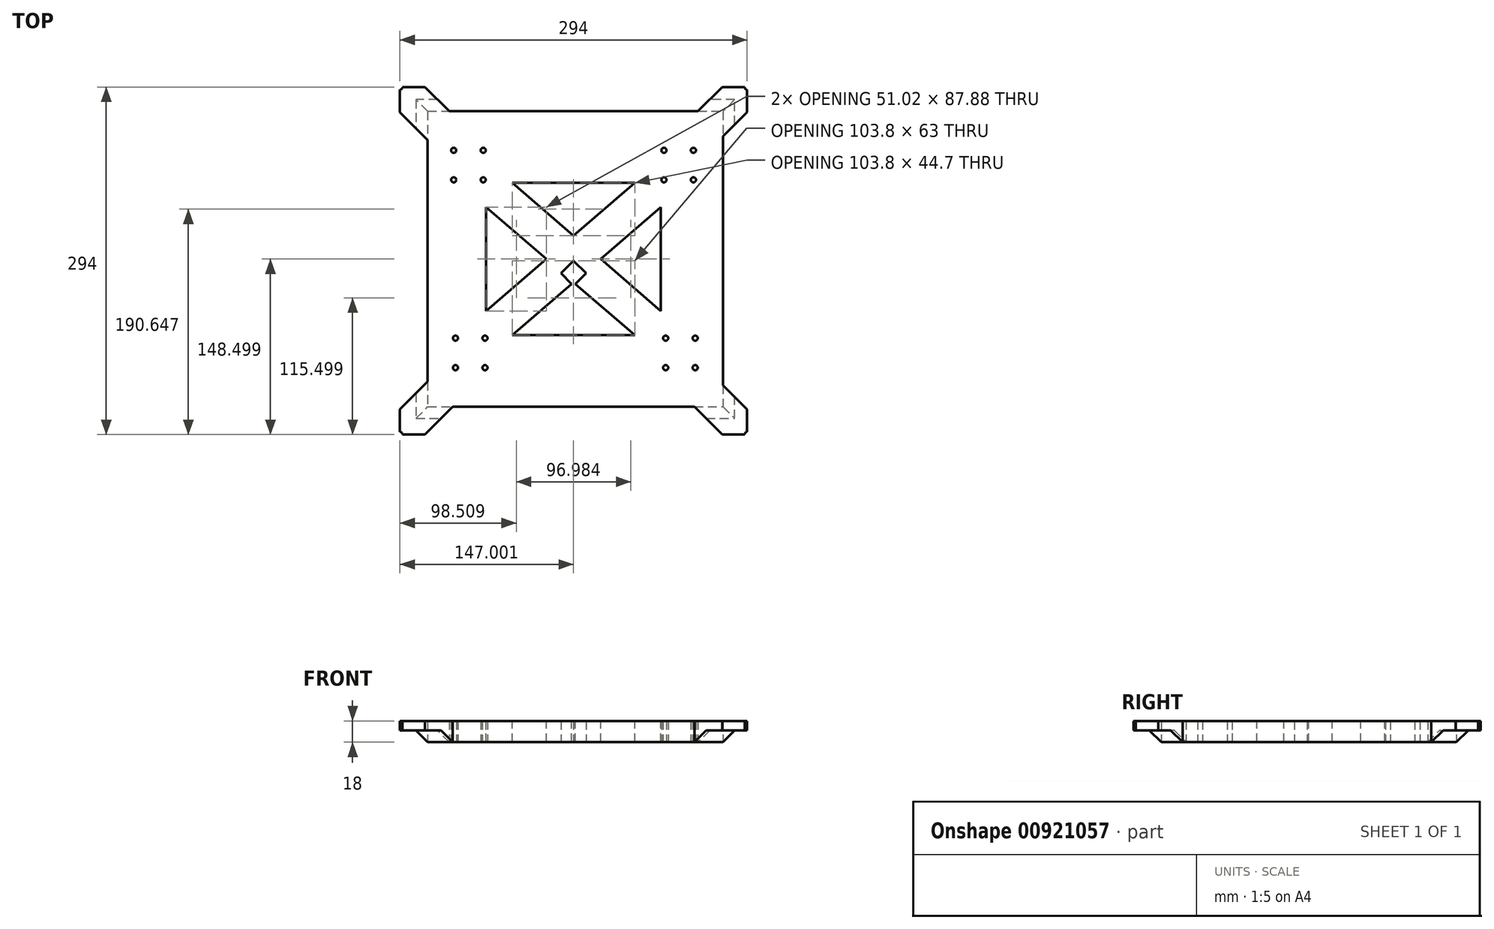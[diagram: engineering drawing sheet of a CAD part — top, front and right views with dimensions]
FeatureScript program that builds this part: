
annotation { "Feature Type Name" : "Feature", "Feature Type Description" : "" }
export const myFeature = defineFeature(function(context is Context, id is Id, definition is map)
    precondition{}
    {
        {
            var Q0;
            Q0=qCreatedBy(makeId("Top.planeOp"),FACE);
            var sketch = newSketch(context, id + "F0", { "sketchPlane" : qUnion([Q0])});
            skLineSegment(sketch, "E0.bottom", {"start": v(-132.57, 169.64) * mm, "end": v(117.43, 169.64) * mm});
            skLineSegment(sketch, "E0.top", {"start": v(-132.57, -80.36) * mm, "end": v(117.43, -80.36) * mm});
            skLineSegment(sketch, "E0.left", {"start": v(-132.57, 169.64) * mm, "end": v(-132.57, -80.36) * mm});
            skLineSegment(sketch, "E0.right", {"start": v(117.43, 169.64) * mm, "end": v(117.43, -80.36) * mm});
            skLineSegment(sketch, "E1", {"start": v(-9.07, 43.14) * mm, "end": v(137.93, 190.14) * mm});
            skLineSegment(sketch, "E2", {"start": v(-9.07, 43.14) * mm, "end": v(137.93, -103.86) * mm});
            skLineSegment(sketch, "E3", {"start": v(137.93, -103.86) * mm, "end": v(137.93, 190.14) * mm});
            skLineSegment(sketch, "E4", {"start": v(-9.07, 43.14) * mm, "end": v(-156.07, 190.14) * mm});
            skLineSegment(sketch, "E5", {"start": v(-156.07, 190.14) * mm, "end": v(137.93, 190.14) * mm});
            skLineSegment(sketch, "E6", {"start": v(-9.07, 43.14) * mm, "end": v(-156.07, -103.86) * mm});
            skLineSegment(sketch, "E7", {"start": v(-156.07, -103.86) * mm, "end": v(-156.07, 190.14) * mm});
            skLineSegment(sketch, "E8", {"start": v(-156.07, -103.86) * mm, "end": v(137.93, -103.86) * mm});
            skArc(sketch, "E9.0.startCap", {"start": v(1.54, 53.75) * mm, "mid": v(1.54, 32.53) * mm, "end": v(-19.68, 32.53) * mm});
            skArc(sketch, "E9.0.endCap", {"start": v(-166.68, 179.53) * mm, "mid": v(-166.68, 200.75) * mm, "end": v(-145.46, 200.75) * mm});
            skLineSegment(sketch, "E9.0.left", {"start": v(-19.68, 32.53) * mm, "end": v(-166.68, 179.53) * mm});
            skLineSegment(sketch, "E9.0.right", {"start": v(1.54, 53.75) * mm, "end": v(-145.46, 200.75) * mm});
            skArc(sketch, "E10.0.startCap", {"start": v(1.54, 32.53) * mm, "mid": v(-19.68, 32.53) * mm, "end": v(-19.68, 53.75) * mm});
            skArc(sketch, "E10.0.endCap", {"start": v(127.32, 200.75) * mm, "mid": v(148.54, 200.75) * mm, "end": v(148.54, 179.53) * mm});
            skLineSegment(sketch, "E10.0.left", {"start": v(-19.68, 53.75) * mm, "end": v(127.32, 200.75) * mm});
            skLineSegment(sketch, "E10.0.right", {"start": v(1.54, 32.53) * mm, "end": v(148.54, 179.53) * mm});
            skArc(sketch, "E11.0.startCap", {"start": v(-19.68, 32.53) * mm, "mid": v(-19.68, 53.75) * mm, "end": v(1.54, 53.75) * mm});
            skArc(sketch, "E11.0.endCap", {"start": v(148.54, -93.25) * mm, "mid": v(148.54, -114.47) * mm, "end": v(127.32, -114.47) * mm});
            skLineSegment(sketch, "E11.0.left", {"start": v(1.54, 53.75) * mm, "end": v(148.54, -93.25) * mm});
            skLineSegment(sketch, "E11.0.right", {"start": v(-19.68, 32.53) * mm, "end": v(127.32, -114.47) * mm});
            skArc(sketch, "E11.1.startCap", {"start": v(-19.68, 53.75) * mm, "mid": v(1.54, 53.75) * mm, "end": v(1.54, 32.53) * mm});
            skArc(sketch, "E11.1.endCap", {"start": v(-145.46, -114.47) * mm, "mid": v(-166.68, -114.47) * mm, "end": v(-166.68, -93.25) * mm});
            skLineSegment(sketch, "E11.1.left", {"start": v(1.54, 32.53) * mm, "end": v(-145.46, -114.47) * mm});
            skLineSegment(sketch, "E11.1.right", {"start": v(-19.68, 53.75) * mm, "end": v(-166.68, -93.25) * mm});
            skSolve(sketch);
        }
        {
            var Q0;
            {var subQ1=sQuery(id+"F0.wireOp",EDGE,"E0.bottom");var subQ3=sQuery(id+"F0.wireOp",EDGE,"E9.0.right");var subQ4=makeQuery(id+"F0.imprint","INTERSECT",VERTEX,{"derivedFrom":[subQ1,subQ3]});Q0=makeQuery(id+"F0.imprint","IMPRINT",FACE,{"disambiguationData":[TD([[makeQuery(id+"F0.imprint","IMPRINT",EDGE,{"disambiguationData":[TD([[subQ4,1.0]])],"derivedFrom":subQ3}),1.0]])]});}
            var Q1;
            {var subQ1=sQuery(id+"F0.wireOp",EDGE,"E0.left");var subQ3=sQuery(id+"F0.wireOp",EDGE,"E9.0.left");var subQ4=makeQuery(id+"F0.imprint","INTERSECT",VERTEX,{"derivedFrom":[subQ1,subQ3]});Q1=makeQuery(id+"F0.imprint","IMPRINT",FACE,{"disambiguationData":[TD([[makeQuery(id+"F0.imprint","IMPRINT",EDGE,{"disambiguationData":[TD([[subQ4,1.0]])],"derivedFrom":subQ3}),-1.0]])]});}
            var Q2;
            {var subQ1=sQuery(id+"F0.wireOp",EDGE,"E0.bottom");var subQ3=sQuery(id+"F0.wireOp",EDGE,"E10.0.left");var subQ4=makeQuery(id+"F0.imprint","INTERSECT",VERTEX,{"derivedFrom":[subQ1,subQ3]});Q2=makeQuery(id+"F0.imprint","IMPRINT",FACE,{"disambiguationData":[TD([[makeQuery(id+"F0.imprint","IMPRINT",EDGE,{"disambiguationData":[TD([[subQ4,1.0]])],"derivedFrom":subQ3}),-1.0]])]});}
            var Q3;
            {var subQ1=sQuery(id+"F0.wireOp",EDGE,"E0.right");var subQ3=sQuery(id+"F0.wireOp",EDGE,"E10.0.right");var subQ4=makeQuery(id+"F0.imprint","INTERSECT",VERTEX,{"derivedFrom":[subQ1,subQ3]});Q3=makeQuery(id+"F0.imprint","IMPRINT",FACE,{"disambiguationData":[TD([[makeQuery(id+"F0.imprint","IMPRINT",EDGE,{"disambiguationData":[TD([[subQ4,1.0]])],"derivedFrom":subQ3}),1.0]])]});}
            var Q4;
            {var subQ1=sQuery(id+"F0.wireOp",EDGE,"E0.top");var subQ3=sQuery(id+"F0.wireOp",EDGE,"E11.0.right");var subQ4=makeQuery(id+"F0.imprint","INTERSECT",VERTEX,{"derivedFrom":[subQ1,subQ3]});Q4=makeQuery(id+"F0.imprint","IMPRINT",FACE,{"disambiguationData":[TD([[makeQuery(id+"F0.imprint","IMPRINT",EDGE,{"disambiguationData":[TD([[subQ4,1.0]])],"derivedFrom":subQ3}),1.0]])]});}
            var Q5;
            {var subQ1=sQuery(id+"F0.wireOp",EDGE,"E0.right");var subQ3=sQuery(id+"F0.wireOp",EDGE,"E11.0.left");var subQ4=makeQuery(id+"F0.imprint","INTERSECT",VERTEX,{"derivedFrom":[subQ1,subQ3]});Q5=makeQuery(id+"F0.imprint","IMPRINT",FACE,{"disambiguationData":[TD([[makeQuery(id+"F0.imprint","IMPRINT",EDGE,{"disambiguationData":[TD([[subQ4,1.0]])],"derivedFrom":subQ3}),-1.0]])]});}
            var Q6;
            {var subQ0=sQuery(id+"F0.wireOp",EDGE,"E10.0.startCap");Q6=makeQuery(id+"F0.imprint","IMPRINT",FACE,{"disambiguationData":[TD([[makeQuery(id+"F0.imprint","IMPRINT",EDGE,{"derivedFrom":subQ0}),1.0]])]});}
            var Q7;
            {var subQ3=sQuery(id+"F0.wireOp",EDGE,"E11.0.startCap");Q7=makeQuery(id+"F0.imprint","IMPRINT",FACE,{"disambiguationData":[TD([[makeQuery(id+"F0.imprint","IMPRINT",EDGE,{"derivedFrom":subQ3}),-1.0]])]});}
            var Q8;
            {var subQ1=sQuery(id+"F0.wireOp",EDGE,"E9.0.right");var subQ3=sQuery(id+"F0.wireOp",EDGE,"E10.0.left");var subQ4=makeQuery(id+"F0.imprint","INTERSECT",VERTEX,{"derivedFrom":[subQ1,subQ3]});Q8=makeQuery(id+"F0.imprint","IMPRINT",FACE,{"disambiguationData":[TD([[makeQuery(id+"F0.imprint","IMPRINT",EDGE,{"disambiguationData":[TD([[subQ4,1.0]])],"derivedFrom":subQ1}),1.0]])]});}
            var Q9;
            {var subQ0=sQuery(id+"F0.wireOp",EDGE,"E2");var subQ1=sQuery(id+"F0.wireOp",EDGE,"E1");var subQ2=makeQuery(id+"F0.imprint","INTERSECT",VERTEX,{"derivedFrom":[subQ1,subQ0,sQuery(id+"F0.wireOp",EDGE,"E4"),sQuery(id+"F0.wireOp",EDGE,"E6")]});Q9=makeQuery(id+"F0.imprint","IMPRINT",FACE,{"disambiguationData":[TD([[makeQuery(id+"F0.imprint","IMPRINT",EDGE,{"disambiguationData":[TD([[subQ2,-1.0]])],"derivedFrom":subQ1}),-1.0]])]});}
            var Q10;
            {var subQ3=sQuery(id+"F0.wireOp",EDGE,"E10.0.startCap");Q10=makeQuery(id+"F0.imprint","IMPRINT",FACE,{"disambiguationData":[TD([[makeQuery(id+"F0.imprint","IMPRINT",EDGE,{"derivedFrom":subQ3}),-1.0]])]});}
            var Q11;
            {var subQ0=sQuery(id+"F0.wireOp",EDGE,"E4");var subQ1=sQuery(id+"F0.wireOp",EDGE,"E1");var subQ2=makeQuery(id+"F0.imprint","INTERSECT",VERTEX,{"derivedFrom":[subQ1,sQuery(id+"F0.wireOp",EDGE,"E2"),subQ0,sQuery(id+"F0.wireOp",EDGE,"E6")]});Q11=makeQuery(id+"F0.imprint","IMPRINT",FACE,{"disambiguationData":[TD([[makeQuery(id+"F0.imprint","IMPRINT",EDGE,{"disambiguationData":[TD([[subQ2,-1.0]])],"derivedFrom":subQ1}),1.0]])]});}
            var Q12;
            {var subQ1=sQuery(id+"F0.wireOp",EDGE,"E10.0.right");var subQ3=sQuery(id+"F0.wireOp",EDGE,"E11.0.left");var subQ4=makeQuery(id+"F0.imprint","INTERSECT",VERTEX,{"derivedFrom":[subQ1,subQ3]});Q12=makeQuery(id+"F0.imprint","IMPRINT",FACE,{"disambiguationData":[TD([[makeQuery(id+"F0.imprint","IMPRINT",EDGE,{"disambiguationData":[TD([[subQ4,1.0]])],"derivedFrom":subQ3}),-1.0]])]});}
            var Q13;
            {var subQ0=sQuery(id+"F0.wireOp",EDGE,"E11.0.startCap");Q13=makeQuery(id+"F0.imprint","IMPRINT",FACE,{"disambiguationData":[TD([[makeQuery(id+"F0.imprint","IMPRINT",EDGE,{"derivedFrom":subQ0}),1.0]])]});}
            var Q14;
            {var subQ1=sQuery(id+"F0.wireOp",EDGE,"E0.top");var subQ3=sQuery(id+"F0.wireOp",EDGE,"E11.1.left");var subQ4=makeQuery(id+"F0.imprint","INTERSECT",VERTEX,{"derivedFrom":[subQ1,subQ3]});Q14=makeQuery(id+"F0.imprint","IMPRINT",FACE,{"disambiguationData":[TD([[makeQuery(id+"F0.imprint","IMPRINT",EDGE,{"disambiguationData":[TD([[subQ4,1.0]])],"derivedFrom":subQ3}),-1.0]])]});}
            var Q15;
            {var subQ1=sQuery(id+"F0.wireOp",EDGE,"E0.left");var subQ3=sQuery(id+"F0.wireOp",EDGE,"E11.1.right");var subQ4=makeQuery(id+"F0.imprint","INTERSECT",VERTEX,{"derivedFrom":[subQ1,subQ3]});Q15=makeQuery(id+"F0.imprint","IMPRINT",FACE,{"disambiguationData":[TD([[makeQuery(id+"F0.imprint","IMPRINT",EDGE,{"disambiguationData":[TD([[subQ4,1.0]])],"derivedFrom":subQ3}),1.0]])]});}
            var Q16;
            {var subQ1=sQuery(id+"F0.wireOp",EDGE,"E9.0.endCap");Q16=makeQuery(id+"F0.imprint","IMPRINT",FACE,{"disambiguationData":[TD([[makeQuery(id+"F0.imprint","IMPRINT",EDGE,{"derivedFrom":subQ1}),-1.0]])]});}
            var Q17;
            {var subQ3=sQuery(id+"F0.wireOp",EDGE,"E9.0.left");var subQ5=sQuery(id+"F0.wireOp",EDGE,"E7");var subQ7=makeQuery(id+"F0.imprint","INTERSECT",VERTEX,{"derivedFrom":[subQ5,subQ3]});Q17=makeQuery(id+"F0.imprint","IMPRINT",FACE,{"disambiguationData":[TD([[makeQuery(id+"F0.imprint","IMPRINT",EDGE,{"disambiguationData":[TD([[subQ7,1.0]])],"derivedFrom":subQ3}),-1.0]])]});}
            var Q18;
            {var subQ3=sQuery(id+"F0.wireOp",EDGE,"E9.0.right");var subQ5=sQuery(id+"F0.wireOp",EDGE,"E5");var subQ7=makeQuery(id+"F0.imprint","INTERSECT",VERTEX,{"derivedFrom":[subQ5,subQ3]});Q18=makeQuery(id+"F0.imprint","IMPRINT",FACE,{"disambiguationData":[TD([[makeQuery(id+"F0.imprint","IMPRINT",EDGE,{"disambiguationData":[TD([[subQ7,1.0]])],"derivedFrom":subQ3}),1.0]])]});}
            var Q19;
            {var subQ0=sQuery(id+"F0.wireOp",EDGE,"E10.0.endCap");Q19=makeQuery(id+"F0.imprint","IMPRINT",FACE,{"disambiguationData":[TD([[makeQuery(id+"F0.imprint","IMPRINT",EDGE,{"derivedFrom":subQ0}),-1.0]])]});}
            var Q20;
            {var subQ3=sQuery(id+"F0.wireOp",EDGE,"E10.0.left");var subQ5=sQuery(id+"F0.wireOp",EDGE,"E5");var subQ7=makeQuery(id+"F0.imprint","INTERSECT",VERTEX,{"derivedFrom":[subQ5,subQ3]});Q20=makeQuery(id+"F0.imprint","IMPRINT",FACE,{"disambiguationData":[TD([[makeQuery(id+"F0.imprint","IMPRINT",EDGE,{"disambiguationData":[TD([[subQ7,1.0]])],"derivedFrom":subQ3}),-1.0]])]});}
            var Q21;
            {var subQ3=sQuery(id+"F0.wireOp",EDGE,"E10.0.right");var subQ5=sQuery(id+"F0.wireOp",EDGE,"E3");var subQ7=makeQuery(id+"F0.imprint","INTERSECT",VERTEX,{"derivedFrom":[subQ5,subQ3]});Q21=makeQuery(id+"F0.imprint","IMPRINT",FACE,{"disambiguationData":[TD([[makeQuery(id+"F0.imprint","IMPRINT",EDGE,{"disambiguationData":[TD([[subQ7,1.0]])],"derivedFrom":subQ3}),1.0]])]});}
            var Q22;
            {var subQ3=sQuery(id+"F0.wireOp",EDGE,"E11.0.left");var subQ5=sQuery(id+"F0.wireOp",EDGE,"E3");var subQ7=makeQuery(id+"F0.imprint","INTERSECT",VERTEX,{"derivedFrom":[subQ5,subQ3]});Q22=makeQuery(id+"F0.imprint","IMPRINT",FACE,{"disambiguationData":[TD([[makeQuery(id+"F0.imprint","IMPRINT",EDGE,{"disambiguationData":[TD([[subQ7,1.0]])],"derivedFrom":subQ3}),-1.0]])]});}
            var Q23;
            {var subQ3=sQuery(id+"F0.wireOp",EDGE,"E11.0.right");var subQ5=sQuery(id+"F0.wireOp",EDGE,"E8");var subQ7=makeQuery(id+"F0.imprint","INTERSECT",VERTEX,{"derivedFrom":[subQ5,subQ3]});Q23=makeQuery(id+"F0.imprint","IMPRINT",FACE,{"disambiguationData":[TD([[makeQuery(id+"F0.imprint","IMPRINT",EDGE,{"disambiguationData":[TD([[subQ7,1.0]])],"derivedFrom":subQ3}),1.0]])]});}
            var Q24;
            {var subQ0=sQuery(id+"F0.wireOp",EDGE,"E11.0.endCap");Q24=makeQuery(id+"F0.imprint","IMPRINT",FACE,{"disambiguationData":[TD([[makeQuery(id+"F0.imprint","IMPRINT",EDGE,{"derivedFrom":subQ0}),-1.0]])]});}
            var Q25;
            {var subQ1=sQuery(id+"F0.wireOp",EDGE,"E11.1.endCap");Q25=makeQuery(id+"F0.imprint","IMPRINT",FACE,{"disambiguationData":[TD([[makeQuery(id+"F0.imprint","IMPRINT",EDGE,{"derivedFrom":subQ1}),-1.0]])]});}
            var Q26;
            {var subQ3=sQuery(id+"F0.wireOp",EDGE,"E11.1.left");var subQ5=sQuery(id+"F0.wireOp",EDGE,"E8");var subQ7=makeQuery(id+"F0.imprint","INTERSECT",VERTEX,{"derivedFrom":[subQ5,subQ3]});Q26=makeQuery(id+"F0.imprint","IMPRINT",FACE,{"disambiguationData":[TD([[makeQuery(id+"F0.imprint","IMPRINT",EDGE,{"disambiguationData":[TD([[subQ7,1.0]])],"derivedFrom":subQ3}),-1.0]])]});}
            var Q27;
            {var subQ3=sQuery(id+"F0.wireOp",EDGE,"E11.1.right");var subQ5=sQuery(id+"F0.wireOp",EDGE,"E7");var subQ7=makeQuery(id+"F0.imprint","INTERSECT",VERTEX,{"derivedFrom":[subQ5,subQ3]});Q27=makeQuery(id+"F0.imprint","IMPRINT",FACE,{"disambiguationData":[TD([[makeQuery(id+"F0.imprint","IMPRINT",EDGE,{"disambiguationData":[TD([[subQ7,1.0]])],"derivedFrom":subQ3}),1.0]])]});}
            var Q28;
            {var subQ0=sQuery(id+"F0.wireOp",EDGE,"E10.0.right");var subQ1=sQuery(id+"F0.wireOp",EDGE,"E0.right");var subQ2=makeQuery(id+"F0.imprint","INTERSECT",VERTEX,{"derivedFrom":[subQ1,subQ0]});Q28=makeQuery(id+"F0.imprint","IMPRINT",FACE,{"disambiguationData":[TD([[makeQuery(id+"F0.imprint","IMPRINT",EDGE,{"disambiguationData":[TD([[subQ2,-1.0]])],"derivedFrom":subQ1}),-1.0]])]});}
            var Q29;
            {var subQ0=sQuery(id+"F0.wireOp",EDGE,"E11.1.left");var subQ1=sQuery(id+"F0.wireOp",EDGE,"E0.top");var subQ2=makeQuery(id+"F0.imprint","INTERSECT",VERTEX,{"derivedFrom":[subQ1,subQ0]});Q29=makeQuery(id+"F0.imprint","IMPRINT",FACE,{"disambiguationData":[TD([[makeQuery(id+"F0.imprint","IMPRINT",EDGE,{"disambiguationData":[TD([[subQ2,-1.0]])],"derivedFrom":subQ1}),1.0]])]});}
            var Q30;
            {var subQ0=sQuery(id+"F0.wireOp",EDGE,"E9.0.left");var subQ1=sQuery(id+"F0.wireOp",EDGE,"E0.left");var subQ2=makeQuery(id+"F0.imprint","INTERSECT",VERTEX,{"derivedFrom":[subQ1,subQ0]});Q30=makeQuery(id+"F0.imprint","IMPRINT",FACE,{"disambiguationData":[TD([[makeQuery(id+"F0.imprint","IMPRINT",EDGE,{"disambiguationData":[TD([[subQ2,-1.0]])],"derivedFrom":subQ1}),1.0]])]});}
            var Q31;
            {var subQ0=sQuery(id+"F0.wireOp",EDGE,"E9.0.right");var subQ1=sQuery(id+"F0.wireOp",EDGE,"E0.bottom");var subQ2=makeQuery(id+"F0.imprint","INTERSECT",VERTEX,{"derivedFrom":[subQ1,subQ0]});Q31=makeQuery(id+"F0.imprint","IMPRINT",FACE,{"disambiguationData":[TD([[makeQuery(id+"F0.imprint","IMPRINT",EDGE,{"disambiguationData":[TD([[subQ2,-1.0]])],"derivedFrom":subQ1}),-1.0]])]});}
            extrude(context, id + "F1", {"entities" : qUnion([Q0, Q1, Q2, Q3, Q4, Q5, Q6, Q7, Q8, Q9, Q10, Q11, Q12, Q13, Q14, Q15, Q16, Q17, Q18, Q19, Q20, Q21, Q22, Q23, Q24, Q25, Q26, Q27, Q28, Q29, Q30, Q31]), "depth" : 18 * mm, "offsetDistance" : 25 * mm});
        }
        {
            var Q0;
            Q0=makeQuery(id+"F1.opExtrude","CAP_FACE",FACE,{"disambiguationData":[OSD([sQuery(id+"F0.wireOp",EDGE,"E0.bottom"),sQuery(id+"F0.wireOp",EDGE,"E0.top"),sQuery(id+"F0.wireOp",EDGE,"E0.left"),sQuery(id+"F0.wireOp",EDGE,"E0.right")])],"isStart":false});
            var sketch = newSketch(context, id + "F2", { "sketchPlane" : qUnion([Q0])});
            skLineSegment(sketch, "E12.left", {"start": v(-118.57, 144.64) * mm, "end": v(-118.57, -55.36) * mm});
            skLineSegment(sketch, "E12.right", {"start": v(100.43, 144.64) * mm, "end": v(100.43, -55.36) * mm});
            skLineSegment(sketch, "E13", {"start": v(-9.07, 169.64) * mm, "end": v(-9.07, 169.64) * mm});
            skLineSegment(sketch, "E14.bottom", {"start": v(-118.57, 144.64) * mm, "end": v(-77.57, 144.64) * mm});
            skLineSegment(sketch, "E14.top", {"start": v(-118.57, 103.64) * mm, "end": v(-77.57, 103.64) * mm});
            skLineSegment(sketch, "E14.left", {"start": v(-118.57, 144.64) * mm, "end": v(-118.57, 103.64) * mm});
            skLineSegment(sketch, "E14.right", {"start": v(-77.57, 144.64) * mm, "end": v(-77.57, 103.64) * mm});
            skLineSegment(sketch, "E15.bottom", {"start": v(-110.57, 136.64) * mm, "end": v(-85.57, 136.64) * mm});
            skLineSegment(sketch, "E15.top", {"start": v(-110.57, 111.64) * mm, "end": v(-85.57, 111.64) * mm});
            skLineSegment(sketch, "E15.left", {"start": v(-110.57, 136.64) * mm, "end": v(-110.57, 111.64) * mm});
            skLineSegment(sketch, "E15.right", {"start": v(-85.57, 136.64) * mm, "end": v(-85.57, 111.64) * mm});
            skLineSegment(sketch, "E16", {"start": v(-9.07, 169.64) * mm, "end": v(-9.07, 44.64) * mm, "construction": true});
            skLineSegment(sketch, "E17.MirrorCS", {"start": v(100.43, 144.64) * mm, "end": v(100.43, 103.64) * mm});
            skLineSegment(sketch, "E18.MirrorCS", {"start": v(92.43, 136.64) * mm, "end": v(92.43, 111.64) * mm});
            skLineSegment(sketch, "E19.MirrorCS", {"start": v(92.43, 136.64) * mm, "end": v(67.43, 136.64) * mm});
            skLineSegment(sketch, "E20.MirrorCS", {"start": v(92.43, 111.64) * mm, "end": v(67.43, 111.64) * mm});
            skLineSegment(sketch, "E21.MirrorCS", {"start": v(100.43, 103.64) * mm, "end": v(59.43, 103.64) * mm});
            skLineSegment(sketch, "E22.MirrorCS", {"start": v(67.43, 136.64) * mm, "end": v(67.43, 111.64) * mm});
            skLineSegment(sketch, "E23.MirrorCS", {"start": v(100.43, 144.64) * mm, "end": v(59.43, 144.64) * mm});
            skLineSegment(sketch, "E24.MirrorCS", {"start": v(59.43, 144.64) * mm, "end": v(59.43, 103.64) * mm});
            skLineSegment(sketch, "E25.MirrorCS", {"start": v(100.43, 144.64) * mm, "end": v(-118.57, 144.64) * mm});
            skLineSegment(sketch, "E26.MirrorCS", {"start": v(100.43, -55.36) * mm, "end": v(-118.57, -55.36) * mm});
            skLineSegment(sketch, "E27.MirrorCS", {"start": v(93.93, -47.36) * mm, "end": v(93.93, -22.36) * mm});
            skLineSegment(sketch, "E28.MirrorCS", {"start": v(-118.57, -14.36) * mm, "end": v(-77.57, -14.36) * mm});
            skLineSegment(sketch, "E29.MirrorCS", {"start": v(100.43, -55.36) * mm, "end": v(100.43, -14.36) * mm});
            skLineSegment(sketch, "E30.MirrorCS", {"start": v(-109.07, -22.36) * mm, "end": v(-84.07, -22.36) * mm});
            skLineSegment(sketch, "E31.MirrorCS", {"start": v(93.93, -22.36) * mm, "end": v(68.93, -22.36) * mm});
            skLineSegment(sketch, "E32.MirrorCS", {"start": v(-74.57, -55.36) * mm, "end": v(-77.57, -14.36) * mm});
            skLineSegment(sketch, "E33.MirrorCS", {"start": v(-118.57, -55.36) * mm, "end": v(100.43, -55.36) * mm});
            skLineSegment(sketch, "E34.MirrorCS", {"start": v(-84.07, -47.36) * mm, "end": v(-84.07, -22.36) * mm});
            skLineSegment(sketch, "E35.MirrorCS", {"start": v(-118.57, -55.36) * mm, "end": v(-118.57, -14.36) * mm});
            skLineSegment(sketch, "E36.MirrorCS", {"start": v(-118.57, -55.36) * mm, "end": v(-74.57, -55.36) * mm});
            skLineSegment(sketch, "E37.MirrorCS", {"start": v(-109.07, -47.36) * mm, "end": v(-84.07, -47.36) * mm});
            skLineSegment(sketch, "E38.MirrorCS", {"start": v(100.43, -55.36) * mm, "end": v(62.43, -55.36) * mm});
            skLineSegment(sketch, "E39.MirrorCS", {"start": v(93.93, -47.36) * mm, "end": v(68.93, -47.36) * mm});
            skLineSegment(sketch, "E40.MirrorCS", {"start": v(-109.07, -47.36) * mm, "end": v(-109.07, -22.36) * mm});
            skLineSegment(sketch, "E41.MirrorCS", {"start": v(100.43, -14.36) * mm, "end": v(59.43, -14.36) * mm});
            skLineSegment(sketch, "E42.MirrorCS", {"start": v(68.93, -47.36) * mm, "end": v(68.93, -22.36) * mm});
            skLineSegment(sketch, "E43.MirrorCS", {"start": v(62.43, -55.36) * mm, "end": v(59.43, -14.36) * mm});
            skLineSegment(sketch, "E44", {"start": v(79.93, -14.36) * mm, "end": v(79.93, 103.64) * mm, "construction": true});
            skLineSegment(sketch, "E45", {"start": v(79.93, 103.64) * mm, "end": v(59.43, 124.14) * mm, "construction": true});
            skLineSegment(sketch, "E46", {"start": v(59.43, 124.14) * mm, "end": v(-77.57, 124.14) * mm, "construction": true});
            skLineSegment(sketch, "E47", {"start": v(-77.57, 124.14) * mm, "end": v(-98.07, 103.64) * mm, "construction": true});
            skLineSegment(sketch, "E48", {"start": v(-98.07, 103.64) * mm, "end": v(-98.07, -14.36) * mm, "construction": true});
            skLineSegment(sketch, "E49", {"start": v(-98.07, -14.36) * mm, "end": v(-76.07, -34.86) * mm, "construction": true});
            skLineSegment(sketch, "E50", {"start": v(-76.07, -34.86) * mm, "end": v(60.93, -34.86) * mm, "construction": true});
            skLineSegment(sketch, "E51", {"start": v(60.93, -34.86) * mm, "end": v(79.93, -14.36) * mm, "construction": true});
            skArc(sketch, "E52.0.startCap", {"start": v(94.93, -14.36) * mm, "mid": v(79.93, -29.36) * mm, "end": v(64.93, -14.36) * mm});
            skArc(sketch, "E52.0.endCap", {"start": v(64.93, 103.64) * mm, "mid": v(79.93, 118.64) * mm, "end": v(94.93, 103.64) * mm});
            skLineSegment(sketch, "E52.0.left", {"start": v(64.93, -14.36) * mm, "end": v(64.93, 103.64) * mm});
            skLineSegment(sketch, "E52.0.right", {"start": v(94.93, -14.36) * mm, "end": v(94.93, 103.64) * mm});
            skArc(sketch, "E52.1.startCap", {"start": v(59.43, 139.14) * mm, "mid": v(74.43, 124.14) * mm, "end": v(59.43, 109.14) * mm});
            skArc(sketch, "E52.1.endCap", {"start": v(-77.57, 109.14) * mm, "mid": v(-92.57, 124.14) * mm, "end": v(-77.57, 139.14) * mm});
            skLineSegment(sketch, "E52.1.left", {"start": v(59.43, 109.14) * mm, "end": v(-77.57, 109.14) * mm});
            skLineSegment(sketch, "E52.1.right", {"start": v(59.43, 139.14) * mm, "end": v(-77.57, 139.14) * mm});
            skArc(sketch, "E52.2.startCap", {"start": v(-113.07, 103.64) * mm, "mid": v(-98.07, 118.64) * mm, "end": v(-83.07, 103.64) * mm});
            skArc(sketch, "E52.2.endCap", {"start": v(-83.07, -14.36) * mm, "mid": v(-98.07, -29.36) * mm, "end": v(-113.07, -14.36) * mm});
            skLineSegment(sketch, "E52.2.left", {"start": v(-83.07, 103.64) * mm, "end": v(-83.07, -14.36) * mm});
            skLineSegment(sketch, "E52.2.right", {"start": v(-113.07, 103.64) * mm, "end": v(-113.07, -14.36) * mm});
            skArc(sketch, "E52.3.startCap", {"start": v(-76.07, -49.86) * mm, "mid": v(-91.07, -34.86) * mm, "end": v(-76.07, -19.86) * mm});
            skArc(sketch, "E52.3.endCap", {"start": v(60.93, -19.86) * mm, "mid": v(75.93, -34.86) * mm, "end": v(60.93, -49.86) * mm});
            skLineSegment(sketch, "E52.3.left", {"start": v(-76.07, -19.86) * mm, "end": v(60.93, -19.86) * mm});
            skLineSegment(sketch, "E52.3.right", {"start": v(-76.07, -49.86) * mm, "end": v(60.93, -49.86) * mm});
            skLineSegment(sketch, "E53", {"start": v(59.43, -14.36) * mm, "end": v(-77.57, 103.64) * mm, "construction": true});
            skLineSegment(sketch, "E54", {"start": v(-77.57, -14.36) * mm, "end": v(59.43, 103.64) * mm, "construction": true});
            skLineSegment(sketch, "E55", {"start": v(59.43, 103.64) * mm, "end": v(59.43, -14.36) * mm});
            skLineSegment(sketch, "E56", {"start": v(59.43, -14.36) * mm, "end": v(-77.57, -14.36) * mm});
            skLineSegment(sketch, "E57", {"start": v(-77.57, -14.36) * mm, "end": v(-77.57, 103.64) * mm});
            skLineSegment(sketch, "E58", {"start": v(-77.57, 103.64) * mm, "end": v(59.43, 103.64) * mm});
            skPoint(sketch, "E59.orphan", {"position": v(100.43, -80.36) * mm});
            skPoint(sketch, "E60.orphan", {"position": v(-118.57, -80.36) * mm});
            skArc(sketch, "E61.0.startCap", {"start": v(69.22, -3) * mm, "mid": v(70.8, -24.15) * mm, "end": v(49.64, -25.73) * mm});
            skArc(sketch, "E61.0.endCap", {"start": v(-87.36, 92.27) * mm, "mid": v(-88.93, 113.43) * mm, "end": v(-67.78, 115) * mm});
            skLineSegment(sketch, "E61.0.left", {"start": v(49.64, -25.73) * mm, "end": v(-87.36, 92.27) * mm});
            skLineSegment(sketch, "E61.0.right", {"start": v(69.22, -3) * mm, "end": v(-67.78, 115) * mm});
            skArc(sketch, "E61.1.startCap", {"start": v(-67.78, -25.73) * mm, "mid": v(-88.93, -24.15) * mm, "end": v(-87.36, -3) * mm});
            skArc(sketch, "E61.1.endCap", {"start": v(49.64, 115) * mm, "mid": v(70.8, 113.43) * mm, "end": v(69.22, 92.27) * mm});
            skLineSegment(sketch, "E61.1.left", {"start": v(-87.36, -3) * mm, "end": v(49.64, 115) * mm});
            skLineSegment(sketch, "E61.1.right", {"start": v(-67.78, -25.73) * mm, "end": v(69.22, 92.27) * mm});
            skSolve(sketch);
        }
        {
            var Q0;
            Q0=sQuery(id+"F2.wireOp",VERTEX,"E15.bottom.start");
            var Q1;
            Q1=sQuery(id+"F2.wireOp",VERTEX,"E15.bottom.end");
            var Q2;
            Q2=sQuery(id+"F2.wireOp",VERTEX,"E15.top.end");
            var Q3;
            Q3=sQuery(id+"F2.wireOp",VERTEX,"E15.top.start");
            var Q4;
            Q4=sQuery(id+"F2.wireOp",VERTEX,"E30.MirrorCS.start");
            var Q5;
            Q5=sQuery(id+"F2.wireOp",VERTEX,"E30.MirrorCS.end");
            var Q6;
            Q6=sQuery(id+"F2.wireOp",VERTEX,"E34.MirrorCS.start");
            var Q7;
            Q7=sQuery(id+"F2.wireOp",VERTEX,"E37.MirrorCS.start");
            var Q8;
            Q8=sQuery(id+"F2.wireOp",VERTEX,"E31.MirrorCS.end");
            var Q9;
            Q9=sQuery(id+"F2.wireOp",VERTEX,"E27.MirrorCS.end");
            var Q10;
            Q10=sQuery(id+"F2.wireOp",VERTEX,"E27.MirrorCS.start");
            var Q11;
            Q11=sQuery(id+"F2.wireOp",VERTEX,"E39.MirrorCS.end");
            var Q12;
            Q12=sQuery(id+"F2.wireOp",VERTEX,"E20.MirrorCS.end");
            var Q13;
            Q13=sQuery(id+"F2.wireOp",VERTEX,"E19.MirrorCS.end");
            var Q14;
            Q14=sQuery(id+"F2.wireOp",VERTEX,"E18.MirrorCS.start");
            var Q15;
            Q15=sQuery(id+"F2.wireOp",VERTEX,"E18.MirrorCS.end");
            var Q16;
            Q16=sQuery(id+"F0.wireOp",VERTEX,"E11.0.endCap.center");
            var Q17;
            Q17=sQuery(id+"F0.wireOp",VERTEX,"E11.1.endCap.center");
            var Q18;
            Q18=sQuery(id+"F0.wireOp",VERTEX,"E9.0.endCap.center");
            var Q19;
            Q19=sQuery(id+"F0.wireOp",VERTEX,"E10.0.endCap.center");
            var Q20;
            Q20=makeQuery(id+"F1.opExtrude","SWEPT_BODY",BODY,{"disambiguationData":[OSD([sQuery(id+"F0.wireOp",EDGE,"E0.bottom"),sQuery(id+"F0.wireOp",EDGE,"E0.top"),sQuery(id+"F0.wireOp",EDGE,"E0.left"),sQuery(id+"F0.wireOp",EDGE,"E0.right")])]});
            hole(context, id + "F3", {"style" : HoleStyle.SIMPLE, "endStyle" : HoleEndStyle.THROUGH, "standardTappedOrClearance" : lookupTablePath({ "fit" : "Close", "standard" : "ISO", "size" : "M4", "type" : "Clearance" }), "standardBlindInLast" : lookupTablePath({ "fit" : "Close", "standard" : "ISO", "size" : "M4", "type" : "Clearance" }), "holeDiameter" : 4.3 * mm, "majorDiameter" : 5 * mm, "tappedDepth" : 12.9 * mm, "tapClearance" : 3, "locations" : qUnion([Q0, Q1, Q2, Q3, Q4, Q5, Q6, Q7, Q8, Q9, Q10, Q11, Q12, Q13, Q14, Q15, Q16, Q17, Q18, Q19]), "scope" : qUnion([Q20])});
        }
        {
            var Q0;
            Q0=sQuery(id+"F0.wireOp",VERTEX,"E9.0.endCap.center");
            var Q1;
            Q1=sQuery(id+"F0.wireOp",VERTEX,"E11.1.endCap.center");
            var Q2;
            Q2=sQuery(id+"F0.wireOp",VERTEX,"E11.0.endCap.center");
            var Q3;
            Q3=sQuery(id+"F0.wireOp",VERTEX,"E10.0.endCap.center");
            var Q4;
            Q4=makeQuery(id+"F1.opExtrude","SWEPT_BODY",BODY,{"disambiguationData":[OSD([sQuery(id+"F0.wireOp",EDGE,"E0.bottom"),sQuery(id+"F0.wireOp",EDGE,"E0.top"),sQuery(id+"F0.wireOp",EDGE,"E0.left"),sQuery(id+"F0.wireOp",EDGE,"E0.right"),sQuery(id+"F0.wireOp",EDGE,"E9.0.endCap"),sQuery(id+"F0.wireOp",EDGE,"E9.0.left"),sQuery(id+"F0.wireOp",EDGE,"E9.0.right"),sQuery(id+"F0.wireOp",EDGE,"E10.0.endCap"),sQuery(id+"F0.wireOp",EDGE,"E10.0.left"),sQuery(id+"F0.wireOp",EDGE,"E10.0.right"),sQuery(id+"F0.wireOp",EDGE,"E11.0.endCap"),sQuery(id+"F0.wireOp",EDGE,"E11.0.left"),sQuery(id+"F0.wireOp",EDGE,"E11.0.right"),sQuery(id+"F0.wireOp",EDGE,"E11.1.endCap"),sQuery(id+"F0.wireOp",EDGE,"E11.1.left"),sQuery(id+"F0.wireOp",EDGE,"E11.1.right")])]});
            hole(context, id + "F4", {"style" : HoleStyle.SIMPLE, "endStyle" : HoleEndStyle.THROUGH, "oppositeDirection" : true, "standardTappedOrClearance" : lookupTablePath({ "fit" : "Close", "standard" : "ISO", "size" : "M4", "type" : "Clearance" }), "standardBlindInLast" : lookupTablePath({ "fit" : "Close", "standard" : "ISO", "size" : "M4", "type" : "Clearance" }), "holeDiameter" : 4.3 * mm, "majorDiameter" : 5 * mm, "tappedDepth" : 12.9 * mm, "tapClearance" : 3, "locations" : qUnion([Q0, Q1, Q2, Q3]), "scope" : qUnion([Q4])});
        }
        {
            var Q0;
            {var subQ3=sQuery(id+"F0.wireOp",EDGE,"E11.0.right");var subQ5=sQuery(id+"F0.wireOp",EDGE,"E8");var subQ7=makeQuery(id+"F0.imprint","INTERSECT",VERTEX,{"derivedFrom":[subQ5,subQ3]});Q0=makeQuery(id+"F0.imprint","IMPRINT",FACE,{"disambiguationData":[TD([[makeQuery(id+"F0.imprint","IMPRINT",EDGE,{"disambiguationData":[TD([[subQ7,1.0]])],"derivedFrom":subQ3}),1.0]])]});}
            var Q1;
            {var subQ3=sQuery(id+"F0.wireOp",EDGE,"E11.0.left");var subQ5=sQuery(id+"F0.wireOp",EDGE,"E3");var subQ7=makeQuery(id+"F0.imprint","INTERSECT",VERTEX,{"derivedFrom":[subQ5,subQ3]});Q1=makeQuery(id+"F0.imprint","IMPRINT",FACE,{"disambiguationData":[TD([[makeQuery(id+"F0.imprint","IMPRINT",EDGE,{"disambiguationData":[TD([[subQ7,1.0]])],"derivedFrom":subQ3}),-1.0]])]});}
            var Q2;
            {var subQ0=sQuery(id+"F0.wireOp",EDGE,"E11.0.endCap");Q2=makeQuery(id+"F0.imprint","IMPRINT",FACE,{"disambiguationData":[TD([[makeQuery(id+"F0.imprint","IMPRINT",EDGE,{"derivedFrom":subQ0}),-1.0]])]});}
            var Q3;
            {var subQ3=sQuery(id+"F0.wireOp",EDGE,"E10.0.right");var subQ5=sQuery(id+"F0.wireOp",EDGE,"E3");var subQ7=makeQuery(id+"F0.imprint","INTERSECT",VERTEX,{"derivedFrom":[subQ5,subQ3]});Q3=makeQuery(id+"F0.imprint","IMPRINT",FACE,{"disambiguationData":[TD([[makeQuery(id+"F0.imprint","IMPRINT",EDGE,{"disambiguationData":[TD([[subQ7,1.0]])],"derivedFrom":subQ3}),1.0]])]});}
            var Q4;
            {var subQ3=sQuery(id+"F0.wireOp",EDGE,"E10.0.left");var subQ5=sQuery(id+"F0.wireOp",EDGE,"E5");var subQ7=makeQuery(id+"F0.imprint","INTERSECT",VERTEX,{"derivedFrom":[subQ5,subQ3]});Q4=makeQuery(id+"F0.imprint","IMPRINT",FACE,{"disambiguationData":[TD([[makeQuery(id+"F0.imprint","IMPRINT",EDGE,{"disambiguationData":[TD([[subQ7,1.0]])],"derivedFrom":subQ3}),-1.0]])]});}
            var Q5;
            {var subQ0=sQuery(id+"F0.wireOp",EDGE,"E10.0.endCap");Q5=makeQuery(id+"F0.imprint","IMPRINT",FACE,{"disambiguationData":[TD([[makeQuery(id+"F0.imprint","IMPRINT",EDGE,{"derivedFrom":subQ0}),-1.0]])]});}
            var Q6;
            {var subQ3=sQuery(id+"F0.wireOp",EDGE,"E9.0.right");var subQ5=sQuery(id+"F0.wireOp",EDGE,"E5");var subQ7=makeQuery(id+"F0.imprint","INTERSECT",VERTEX,{"derivedFrom":[subQ5,subQ3]});Q6=makeQuery(id+"F0.imprint","IMPRINT",FACE,{"disambiguationData":[TD([[makeQuery(id+"F0.imprint","IMPRINT",EDGE,{"disambiguationData":[TD([[subQ7,1.0]])],"derivedFrom":subQ3}),1.0]])]});}
            var Q7;
            {var subQ3=sQuery(id+"F0.wireOp",EDGE,"E9.0.left");var subQ5=sQuery(id+"F0.wireOp",EDGE,"E7");var subQ7=makeQuery(id+"F0.imprint","INTERSECT",VERTEX,{"derivedFrom":[subQ5,subQ3]});Q7=makeQuery(id+"F0.imprint","IMPRINT",FACE,{"disambiguationData":[TD([[makeQuery(id+"F0.imprint","IMPRINT",EDGE,{"disambiguationData":[TD([[subQ7,1.0]])],"derivedFrom":subQ3}),-1.0]])]});}
            var Q8;
            {var subQ1=sQuery(id+"F0.wireOp",EDGE,"E9.0.endCap");Q8=makeQuery(id+"F0.imprint","IMPRINT",FACE,{"disambiguationData":[TD([[makeQuery(id+"F0.imprint","IMPRINT",EDGE,{"derivedFrom":subQ1}),-1.0]])]});}
            var Q9;
            {var subQ1=sQuery(id+"F0.wireOp",EDGE,"E11.1.endCap");Q9=makeQuery(id+"F0.imprint","IMPRINT",FACE,{"disambiguationData":[TD([[makeQuery(id+"F0.imprint","IMPRINT",EDGE,{"derivedFrom":subQ1}),-1.0]])]});}
            var Q10;
            {var subQ3=sQuery(id+"F0.wireOp",EDGE,"E11.1.left");var subQ5=sQuery(id+"F0.wireOp",EDGE,"E8");var subQ7=makeQuery(id+"F0.imprint","INTERSECT",VERTEX,{"derivedFrom":[subQ5,subQ3]});Q10=makeQuery(id+"F0.imprint","IMPRINT",FACE,{"disambiguationData":[TD([[makeQuery(id+"F0.imprint","IMPRINT",EDGE,{"disambiguationData":[TD([[subQ7,1.0]])],"derivedFrom":subQ3}),-1.0]])]});}
            var Q11;
            {var subQ3=sQuery(id+"F0.wireOp",EDGE,"E11.1.right");var subQ5=sQuery(id+"F0.wireOp",EDGE,"E7");var subQ7=makeQuery(id+"F0.imprint","INTERSECT",VERTEX,{"derivedFrom":[subQ5,subQ3]});Q11=makeQuery(id+"F0.imprint","IMPRINT",FACE,{"disambiguationData":[TD([[makeQuery(id+"F0.imprint","IMPRINT",EDGE,{"disambiguationData":[TD([[subQ7,1.0]])],"derivedFrom":subQ3}),1.0]])]});}
            extrude(context, id + "F5", {"entities" : qUnion([Q0, Q1, Q2, Q3, Q4, Q5, Q6, Q7, Q8, Q9, Q10, Q11]), "operationType" : NewBodyOperationType.REMOVE, "depth" : 10 * mm, "offsetDistance" : 25 * mm});
        }
        {
            var Q0;
            {var subQ0=sQuery(id+"F0.wireOp",EDGE,"E0.right");Q0=makeQuery(id+"F5.boolean.opBoolean","COPY",EDGE,{"derivedFrom":makeQuery(id+"F5.opExtrude","CAP_EDGE",EDGE,{"disambiguationData":[OSD([subQ0]),TDD([makeQuery(id+"F0.imprint","IMPRINT",EDGE,{"disambiguationData":[TD([[makeQuery(id+"F0.imprint","INTERSECT",VERTEX,{"derivedFrom":[subQ0,sQuery(id+"F0.wireOp",EDGE,"E11.0.left")]}),-1.0]])],"derivedFrom":subQ0})])],"isStart":false})});}
            var Q1;
            {var subQ0=sQuery(id+"F0.wireOp",EDGE,"E0.top");Q1=makeQuery(id+"F5.boolean.opBoolean","COPY",EDGE,{"derivedFrom":makeQuery(id+"F5.opExtrude","CAP_EDGE",EDGE,{"disambiguationData":[OSD([subQ0]),TDD([makeQuery(id+"F0.imprint","IMPRINT",EDGE,{"disambiguationData":[TD([[makeQuery(id+"F0.imprint","INTERSECT",VERTEX,{"derivedFrom":[subQ0,sQuery(id+"F0.wireOp",EDGE,"E11.0.right")]}),-1.0]])],"derivedFrom":subQ0})])],"isStart":false})});}
            var Q2;
            {var subQ0=sQuery(id+"F0.wireOp",EDGE,"E0.top");Q2=makeQuery(id+"F5.boolean.opBoolean","COPY",EDGE,{"derivedFrom":makeQuery(id+"F5.opExtrude","CAP_EDGE",EDGE,{"disambiguationData":[OSD([subQ0]),TDD([makeQuery(id+"F0.imprint","IMPRINT",EDGE,{"disambiguationData":[TD([[makeQuery(id+"F0.imprint","INTERSECT",VERTEX,{"derivedFrom":[subQ0,sQuery(id+"F0.wireOp",EDGE,"E11.1.left")]}),1.0]])],"derivedFrom":subQ0})])],"isStart":false})});}
            var Q3;
            {var subQ0=sQuery(id+"F0.wireOp",EDGE,"E0.left");Q3=makeQuery(id+"F5.boolean.opBoolean","COPY",EDGE,{"derivedFrom":makeQuery(id+"F5.opExtrude","CAP_EDGE",EDGE,{"disambiguationData":[OSD([subQ0]),TDD([makeQuery(id+"F0.imprint","IMPRINT",EDGE,{"disambiguationData":[TD([[makeQuery(id+"F0.imprint","INTERSECT",VERTEX,{"derivedFrom":[subQ0,sQuery(id+"F0.wireOp",EDGE,"E11.1.right")]}),-1.0]])],"derivedFrom":subQ0})])],"isStart":false})});}
            var Q4;
            {var subQ0=sQuery(id+"F0.wireOp",EDGE,"E0.left");Q4=makeQuery(id+"F5.boolean.opBoolean","COPY",EDGE,{"derivedFrom":makeQuery(id+"F5.opExtrude","CAP_EDGE",EDGE,{"disambiguationData":[OSD([subQ0]),TDD([makeQuery(id+"F0.imprint","IMPRINT",EDGE,{"disambiguationData":[TD([[makeQuery(id+"F0.imprint","INTERSECT",VERTEX,{"derivedFrom":[subQ0,sQuery(id+"F0.wireOp",EDGE,"E9.0.left")]}),1.0]])],"derivedFrom":subQ0})])],"isStart":false})});}
            var Q5;
            {var subQ0=sQuery(id+"F0.wireOp",EDGE,"E0.bottom");Q5=makeQuery(id+"F5.boolean.opBoolean","COPY",EDGE,{"derivedFrom":makeQuery(id+"F5.opExtrude","CAP_EDGE",EDGE,{"disambiguationData":[OSD([subQ0]),TDD([makeQuery(id+"F0.imprint","IMPRINT",EDGE,{"disambiguationData":[TD([[makeQuery(id+"F0.imprint","INTERSECT",VERTEX,{"derivedFrom":[subQ0,sQuery(id+"F0.wireOp",EDGE,"E9.0.right")]}),1.0]])],"derivedFrom":subQ0})])],"isStart":false})});}
            var Q6;
            {var subQ0=sQuery(id+"F0.wireOp",EDGE,"E0.bottom");Q6=makeQuery(id+"F5.boolean.opBoolean","COPY",EDGE,{"derivedFrom":makeQuery(id+"F5.opExtrude","CAP_EDGE",EDGE,{"disambiguationData":[OSD([subQ0]),TDD([makeQuery(id+"F0.imprint","IMPRINT",EDGE,{"disambiguationData":[TD([[makeQuery(id+"F0.imprint","INTERSECT",VERTEX,{"derivedFrom":[subQ0,sQuery(id+"F0.wireOp",EDGE,"E10.0.left")]}),-1.0]])],"derivedFrom":subQ0})])],"isStart":false})});}
            var Q7;
            {var subQ0=sQuery(id+"F0.wireOp",EDGE,"E0.right");Q7=makeQuery(id+"F5.boolean.opBoolean","COPY",EDGE,{"derivedFrom":makeQuery(id+"F5.opExtrude","CAP_EDGE",EDGE,{"disambiguationData":[OSD([subQ0]),TDD([makeQuery(id+"F0.imprint","IMPRINT",EDGE,{"disambiguationData":[TD([[makeQuery(id+"F0.imprint","INTERSECT",VERTEX,{"derivedFrom":[subQ0,sQuery(id+"F0.wireOp",EDGE,"E10.0.right")]}),1.0]])],"derivedFrom":subQ0})])],"isStart":false})});}
            chamfer(context, id + "F6", {"entities" : qUnion([Q0, Q1, Q2, Q3, Q4, Q5, Q6, Q7]), "chamferType" : ChamferType.TWO_OFFSETS, "width1" : 10 * mm, "oppositeDirection" : false, "width2" : 10 * mm, "tangentPropagation" : true});
        }
        {
            var Q0;
            {var subQ0=sQuery(id+"F2.wireOp",EDGE,"E61.1.right");var subQ1=sQuery(id+"F2.wireOp",EDGE,"E55");var subQ2=makeQuery(id+"F2.imprint","INTERSECT",VERTEX,{"derivedFrom":[subQ1,subQ0]});Q0=makeQuery(id+"F2.imprint","IMPRINT",FACE,{"disambiguationData":[TD([[makeQuery(id+"F2.imprint","IMPRINT",EDGE,{"disambiguationData":[TD([[subQ2,-1.0]])],"derivedFrom":subQ1}),-1.0]])]});}
            var Q1;
            {var subQ0=sQuery(id+"F2.wireOp",EDGE,"E61.0.left");var subQ1=sQuery(id+"F2.wireOp",EDGE,"E56");var subQ2=makeQuery(id+"F2.imprint","INTERSECT",VERTEX,{"derivedFrom":[subQ1,subQ0]});Q1=makeQuery(id+"F2.imprint","IMPRINT",FACE,{"disambiguationData":[TD([[makeQuery(id+"F2.imprint","IMPRINT",EDGE,{"disambiguationData":[TD([[subQ2,-1.0]])],"derivedFrom":subQ1}),-1.0]])]});}
            var Q2;
            {var subQ0=sQuery(id+"F2.wireOp",EDGE,"E61.1.left");var subQ1=sQuery(id+"F2.wireOp",EDGE,"E57");var subQ2=makeQuery(id+"F2.imprint","INTERSECT",VERTEX,{"derivedFrom":[subQ1,subQ0]});Q2=makeQuery(id+"F2.imprint","IMPRINT",FACE,{"disambiguationData":[TD([[makeQuery(id+"F2.imprint","IMPRINT",EDGE,{"disambiguationData":[TD([[subQ2,-1.0]])],"derivedFrom":subQ1}),-1.0]])]});}
            var Q3;
            {var subQ0=sQuery(id+"F2.wireOp",EDGE,"E61.0.right");var subQ1=sQuery(id+"F2.wireOp",EDGE,"E58");var subQ2=makeQuery(id+"F2.imprint","INTERSECT",VERTEX,{"derivedFrom":[subQ1,subQ0]});Q3=makeQuery(id+"F2.imprint","IMPRINT",FACE,{"disambiguationData":[TD([[makeQuery(id+"F2.imprint","IMPRINT",EDGE,{"disambiguationData":[TD([[subQ2,-1.0]])],"derivedFrom":subQ1}),-1.0]])]});}
            var Q4;
            {var subQ0=sQuery(id+"F2.wireOp",EDGE,"E61.1.right");var subQ1=sQuery(id+"F2.wireOp",EDGE,"E52.3.left");var subQ2=makeQuery(id+"F2.imprint","INTERSECT",VERTEX,{"derivedFrom":[subQ1,subQ0]});Q4=makeQuery(id+"F2.imprint","IMPRINT",FACE,{"disambiguationData":[TD([[makeQuery(id+"F2.imprint","IMPRINT",EDGE,{"disambiguationData":[TD([[subQ2,-1.0]])],"derivedFrom":subQ1}),1.0]])]});}
            var Q5;
            {var subQ0=sQuery(id+"F2.wireOp",EDGE,"E61.0.left");var subQ1=sQuery(id+"F2.wireOp",EDGE,"E52.2.left");var subQ2=makeQuery(id+"F2.imprint","INTERSECT",VERTEX,{"derivedFrom":[subQ1,subQ0]});Q5=makeQuery(id+"F2.imprint","IMPRINT",FACE,{"disambiguationData":[TD([[makeQuery(id+"F2.imprint","IMPRINT",EDGE,{"disambiguationData":[TD([[subQ2,-1.0]])],"derivedFrom":subQ1}),1.0]])]});}
            var Q6;
            {var subQ0=sQuery(id+"F2.wireOp",EDGE,"E61.0.right");var subQ1=sQuery(id+"F2.wireOp",EDGE,"E52.0.left");var subQ2=makeQuery(id+"F2.imprint","INTERSECT",VERTEX,{"derivedFrom":[subQ1,subQ0]});Q6=makeQuery(id+"F2.imprint","IMPRINT",FACE,{"disambiguationData":[TD([[makeQuery(id+"F2.imprint","IMPRINT",EDGE,{"disambiguationData":[TD([[subQ2,-1.0]])],"derivedFrom":subQ1}),1.0]])]});}
            var Q7;
            {var subQ0=sQuery(id+"F2.wireOp",EDGE,"E61.1.left");var subQ1=sQuery(id+"F2.wireOp",EDGE,"E52.1.left");var subQ2=makeQuery(id+"F2.imprint","INTERSECT",VERTEX,{"derivedFrom":[subQ1,subQ0]});Q7=makeQuery(id+"F2.imprint","IMPRINT",FACE,{"disambiguationData":[TD([[makeQuery(id+"F2.imprint","IMPRINT",EDGE,{"disambiguationData":[TD([[subQ2,-1.0]])],"derivedFrom":subQ1}),1.0]])]});}
            extrude(context, id + "F7", {"entities" : qUnion([Q0, Q1, Q2, Q3, Q4, Q5, Q6, Q7]), "operationType" : NewBodyOperationType.REMOVE, "oppositeDirection" : true, "depth" : 25 * mm, "offsetDistance" : 25 * mm});
        }
    });
